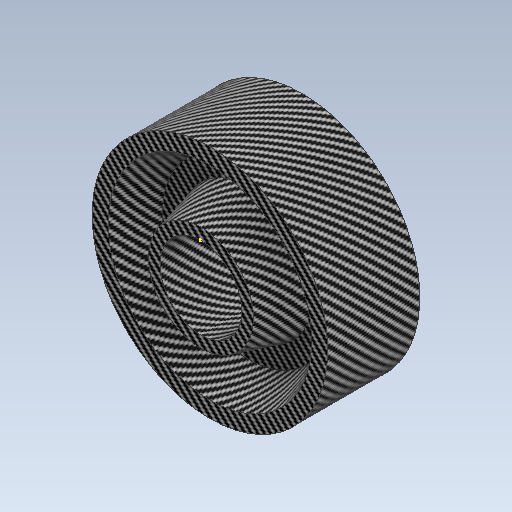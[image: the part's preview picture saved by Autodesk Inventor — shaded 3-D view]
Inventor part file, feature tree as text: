
AUTODESK INVENTOR PART (.ipt)
format: ipt  version: 2021 (Build 250183000, 183)  size: 292,864 bytes
history: native  units: in
note: dims shown in document units (in); Inventor stores cm internally (conversion verified against a paired STEP export)
features: sketch x5, revolve x1
ambient origin geometry x8: Origin, YZ Plane, XZ Plane, XY Plane, X Axis, Y Axis, Z Axis, Center Point
bodies: Solid1 (feature_tree)
feature tree (6):
  sketch  "Sketch1"  dims[d0=1.6929in d1=0.1772in]
  sketch  "Sketch2"  dims[d2=0.1772in]
  sketch  "Sketch3"  dims[d3=1.1811in]
  sketch  "Sketch4"  dims[d4=0.1772in]
  sketch  "Sketch5"  dims[d5=0.1378in d6=1.4173in d7=0.1378in d8=0.7902in d9=75.0deg d11=0.8465in d12=0.0in d13=0.1378in d14=0.2756in d16=0.0in d17=0.0in d29=0.1718in d30=0.1718in d31=0.1031in d32=0.1031in d33=0.5709in d34=0.1378in d35=0.191in d36=0.9065in d37=0.6094in d38=0.2431in d39=0.4032in d40=0.6299in d41=90.0deg]
  revolve  "Revolution1"  [1 undecoded]
note: 1 required parameter value undecoded (feature->parameter linkage not recoverable at this tier; creation-order binding heuristic only, values carry confidence <= 0.55)
